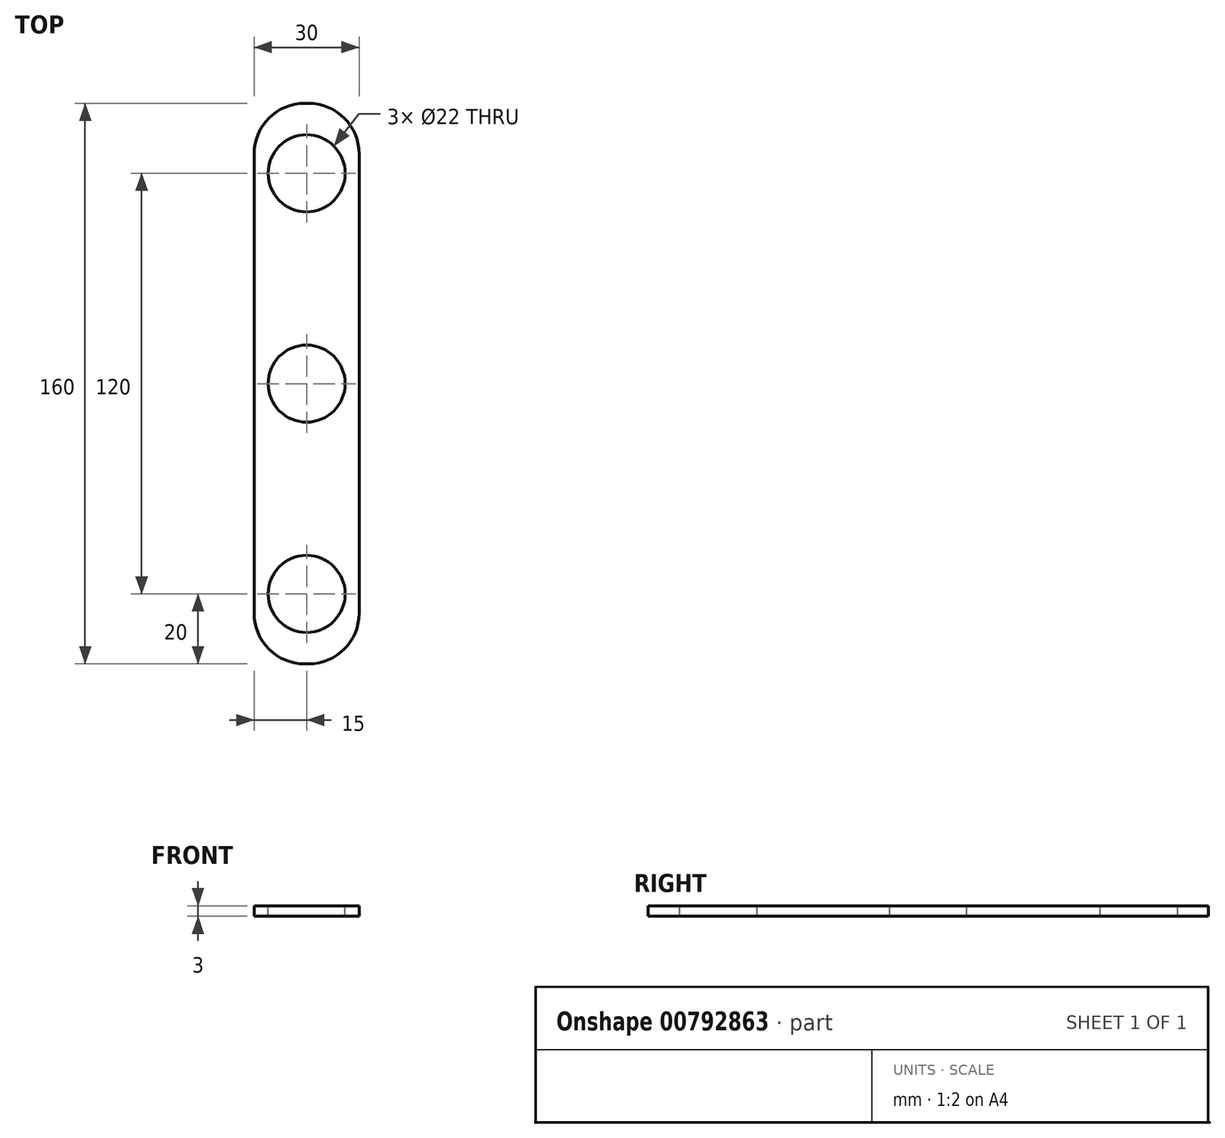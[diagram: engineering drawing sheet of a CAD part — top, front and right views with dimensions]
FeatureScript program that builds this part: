
annotation { "Feature Type Name" : "Feature", "Feature Type Description" : "" }
export const myFeature = defineFeature(function(context is Context, id is Id, definition is map)
    precondition{}
    {
        {
            var Q0;
            Q0=qCreatedBy(makeId("Top.planeOp"),FACE);
            var sketch = newSketch(context, id + "F0", { "sketchPlane" : qUnion([Q0])});
            skLineSegment(sketch, "E0.bottom", {"start": v(-15, -80) * mm, "end": v(15, -80) * mm});
            skLineSegment(sketch, "E0.top", {"start": v(-15, 80) * mm, "end": v(15, 80) * mm});
            skLineSegment(sketch, "E0.left", {"start": v(-15, -80) * mm, "end": v(-15, 80) * mm});
            skLineSegment(sketch, "E0.right", {"start": v(15, -80) * mm, "end": v(15, 80) * mm});
            skPoint(sketch, "E0.middle", {"position": v(0, 0) * mm});
            skSolve(sketch);
        }
        {
            var Q0;
            Q0=makeQuery(id+"F0.imprint","IMPRINT",FACE,{"disambiguationData":[TD([[makeQuery(id+"F0.imprint","IMPRINT",EDGE,{"derivedFrom":sQuery(id+"F0.wireOp",EDGE,"E0.bottom")}),1.0]])]});
            extrude(context, id + "F1", {"entities" : qUnion([Q0]), "depth" : 3 * mm, "offsetDistance" : 25 * mm});
        }
        {
            var Q0;
            Q0=makeQuery(id+"F1.opExtrude","CAP_FACE",FACE,{"disambiguationData":[OSD([sQuery(id+"F0.wireOp",EDGE,"E0.bottom"),sQuery(id+"F0.wireOp",EDGE,"E0.top"),sQuery(id+"F0.wireOp",EDGE,"E0.left"),sQuery(id+"F0.wireOp",EDGE,"E0.right")])],"isStart":false});
            var sketch = newSketch(context, id + "F2", { "sketchPlane" : qUnion([Q0])});
            skCircle(sketch, "E1", {"center": v(0, 0) * mm, "radius": 11 * mm});
            skSolve(sketch);
        }
        {
            var Q0;
            Q0=makeQuery(id+"F2.imprint","IMPRINT",FACE,{"disambiguationData":[TD([[makeQuery(id+"F2.imprint","IMPRINT",EDGE,{"derivedFrom":sQuery(id+"F2.wireOp",EDGE,"E1")}),1.0]])]});
            extrude(context, id + "F3", {"entities" : qUnion([Q0]), "operationType" : NewBodyOperationType.REMOVE, "oppositeDirection" : true, "depth" : 25 * mm, "offsetDistance" : 25 * mm});
        }
        {
            var Q0;
            Q0=qCreatedBy(makeId("Top.planeOp"),FACE);
            var sketch = newSketch(context, id + "F4", { "sketchPlane" : qUnion([Q0])});
            skCircle(sketch, "E2", {"center": v(0, 60) * mm, "radius": 11 * mm});
            skCircle(sketch, "E3", {"center": v(0, -60) * mm, "radius": 11 * mm});
            skSolve(sketch);
        }
        {
            var Q0;
            Q0 = qSketchRegion(id + "F4", true);
            extrude(context, id + "F5", {"entities" : qUnion([Q0]), "operationType" : NewBodyOperationType.REMOVE, "depth" : 25 * mm, "offsetDistance" : 25 * mm});
        }
        {
            var Q0;
            Q0=makeQuery(id+"F1.opExtrude","SWEPT_EDGE",EDGE,{"disambiguationData":[OSD([sQuery(id+"F0.wireOp",EDGE,"E0.bottom"),sQuery(id+"F0.wireOp",EDGE,"E0.left")])]});
            var Q1;
            Q1=makeQuery(id+"F1.opExtrude","SWEPT_EDGE",EDGE,{"disambiguationData":[OSD([sQuery(id+"F0.wireOp",EDGE,"E0.bottom"),sQuery(id+"F0.wireOp",EDGE,"E0.right")])]});
            fillet(context, id + "F6", {"entities" : qUnion([Q0, Q1]), "radius" : 14.5 * mm, "tangentPropagation" : true, "allowEdgeOverflow" : false});
        }
        {
            var Q0;
            Q0=makeQuery(id+"F1.opExtrude","SWEPT_EDGE",EDGE,{"disambiguationData":[OSD([sQuery(id+"F0.wireOp",EDGE,"E0.top"),sQuery(id+"F0.wireOp",EDGE,"E0.left")])]});
            var Q1;
            Q1=makeQuery(id+"F1.opExtrude","SWEPT_EDGE",EDGE,{"disambiguationData":[OSD([sQuery(id+"F0.wireOp",EDGE,"E0.top"),sQuery(id+"F0.wireOp",EDGE,"E0.right")])]});
            fillet(context, id + "F7", {"entities" : qUnion([Q0, Q1]), "radius" : 14.5 * mm, "tangentPropagation" : true, "allowEdgeOverflow" : false});
        }
    });
